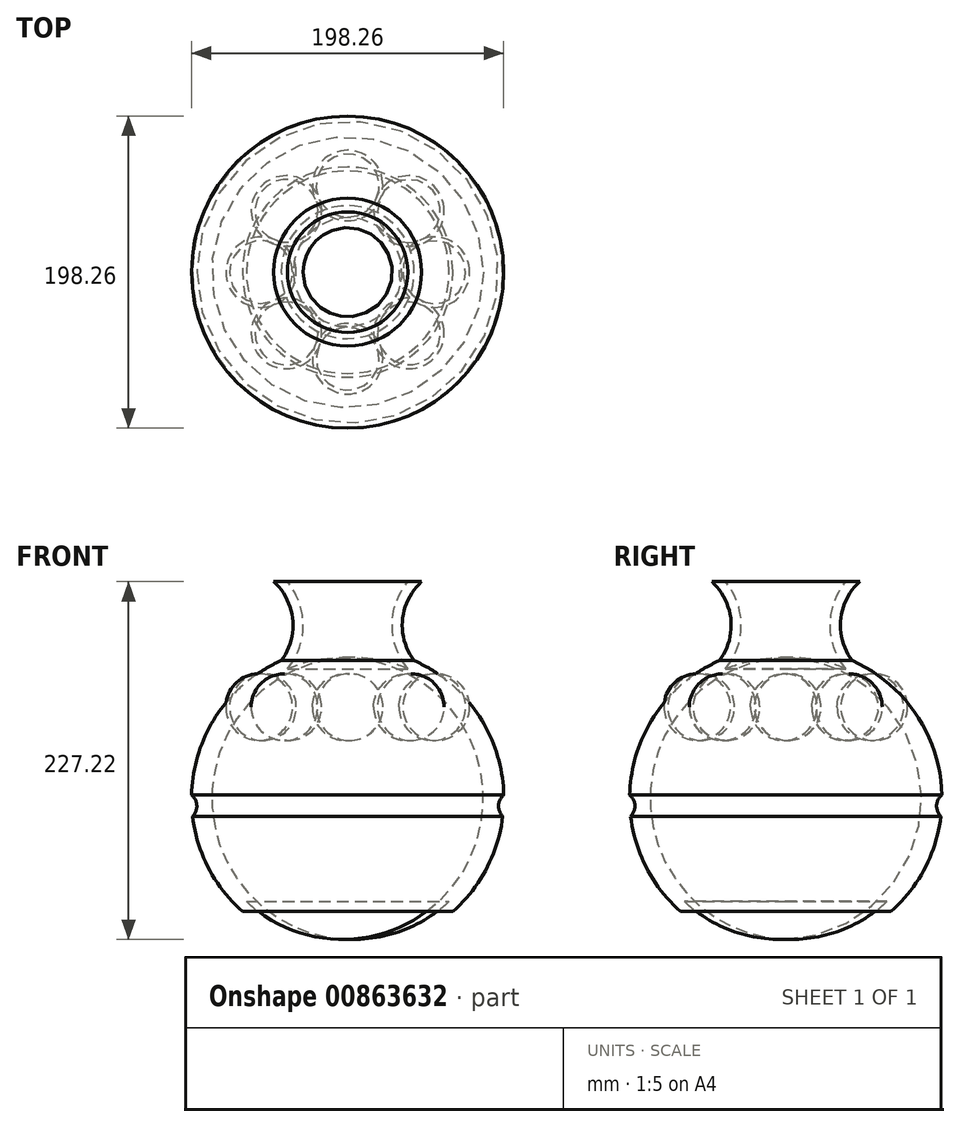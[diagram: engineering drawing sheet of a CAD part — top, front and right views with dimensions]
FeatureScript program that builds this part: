
annotation { "Feature Type Name" : "Feature", "Feature Type Description" : "" }
export const myFeature = defineFeature(function(context is Context, id is Id, definition is map)
    precondition{}
    {
        {
            var Q0;
            Q0=qCreatedBy(makeId("Front.planeOp"),FACE);
            var sketch = newSketch(context, id + "F0", { "sketchPlane" : qUnion([Q0])});
            skLineSegment(sketch, "E0", {"start": v(0, 0) * mm, "end": v(0, 203.2) * mm});
            skLineSegment(sketch, "E1", {"start": v(0, 203.2) * mm, "end": v(38.23, 203.2) * mm});
            skArc(sketch, "E2", {"start": v(38.23, 203.2) * mm, "mid": v(28.32, 175.53) * mm, "end": v(38.23, 147.86) * mm});
            skLineSegment(sketch, "E3", {"start": v(64.33, 0) * mm, "end": v(0, 0) * mm});
            skArc(sketch, "E4", {"start": v(64.33, 0) * mm, "mid": v(91.44, 81.02) * mm, "end": v(38.23, 147.86) * mm});
            skSolve(sketch);
        }
        {
            var Q0;
            Q0 = qSketchRegion(id + "F0", true);
            var Q1;
            Q1=sQuery(id+"F0.wireOp",EDGE,"E0");
            revolve(context, id + "F1", {"surfaceOperationType" : NewSurfaceOperationType.NEW, "entities" : qUnion([Q0]), "axis" : qUnion([Q1]), "revolveType" : RevolveType.FULL});
        }
        {
            var Q0;
            Q0=qCreatedBy(makeId("Front.planeOp"),FACE);
            var sketch = newSketch(context, id + "F2", { "sketchPlane" : qUnion([Q0])});
            skArc(sketch, "E5", {"start": v(176.67, 88.82) * mm, "mid": v(154.28, 67.68) * mm, "end": v(176.67, 46.53) * mm});
            skLineSegment(sketch, "E6", {"start": v(176.67, 88.82) * mm, "end": v(176.67, 46.53) * mm});
            skSolve(sketch);
        }
        {
            var Q0;
            Q0 = qSketchRegion(id + "F2", true);
            var Q1;
            Q1=sQuery(id+"F2.wireOp",EDGE,"E6");
            revolve(context, id + "F3", {"surfaceOperationType" : NewSurfaceOperationType.NEW, "entities" : qUnion([Q0]), "axis" : qUnion([Q1]), "revolveType" : RevolveType.FULL});
        }
        {
            var Q0;
            Q0=makeQuery(id+"F3.opRevolve","SWEPT_BODY",BODY,{"disambiguationData":[OSD([sQuery(id+"F2.wireOp",EDGE,"E5"),sQuery(id+"F2.wireOp",EDGE,"E6")])]});
            transform(context, id + "F4", {"entities" : qUnion([Q0]), "transformType" : TransformType.TRANSLATION_3D, "dx" : -121.67 * mm, "dy" : 0 * mm, "dz" : 55.88 * mm, "makeCopy" : false});
        }
        {
            var Q0;
            Q0=makeQuery(id+"F3.opRevolve","SWEPT_BODY",BODY,{"disambiguationData":[OSD([sQuery(id+"F2.wireOp",EDGE,"E5"),sQuery(id+"F2.wireOp",EDGE,"E6")])]});
            var Q1;
            Q1=makeQuery(id+"F1.opRevolve","SWEPT_EDGE",EDGE,{"disambiguationData":[OSD([sQuery(id+"F0.wireOp",EDGE,"E1"),sQuery(id+"F0.wireOp",EDGE,"E2")])]});
            circularPattern(context, id + "F5", {"entities" : qUnion([Q0]), "axis" : qUnion([Q1]), "angle" : 360 * degree, "instanceCount" : 8, "equalSpace" : true});
        }
        {
            var Q0;
            Q0=makeQuery(id+"F1.opRevolve","SWEPT_FACE",FACE,{"disambiguationData":[OSD([sQuery(id+"F0.wireOp",EDGE,"E1")])]});
            shell(context, id + "F6", {"entities" : qUnion([Q0]), "thickness" : 6.35 * mm, "oppositeDirection" : true});
        }
        {
            var Q0;
            Q0=qCreatedBy(makeId("Front.planeOp"),FACE);
            var sketch = newSketch(context, id + "F7", { "sketchPlane" : qUnion([Q0])});
            skArc(sketch, "E7", {"start": v(110.55, 75.75) * mm, "mid": v(104.23, 69.43) * mm, "end": v(110.55, 63.1) * mm});
            skLineSegment(sketch, "E8", {"start": v(110.55, 75.75) * mm, "end": v(110.55, 63.1) * mm});
            skSolve(sketch);
        }
        {
            var Q0;
            Q0 = qSketchRegion(id + "F7", true);
            var Q1;
            Q1=sQuery(id+"F7.wireOp",EDGE,"E8");
            revolve(context, id + "F8", {"surfaceOperationType" : NewSurfaceOperationType.NEW, "entities" : qUnion([Q0]), "axis" : qUnion([Q1]), "revolveType" : RevolveType.FULL});
        }
        {
            var Q0;
            Q0=makeQuery(id+"F8.opRevolve","SWEPT_BODY",BODY,{"disambiguationData":[OSD([sQuery(id+"F7.wireOp",EDGE,"E7"),sQuery(id+"F7.wireOp",EDGE,"E8")])]});
            transform(context, id + "F9", {"entities" : qUnion([Q0]), "transformType" : TransformType.TRANSLATION_3D, "dx" : -76.2 * mm, "dy" : 0 * mm, "dz" : 105.16 * mm, "makeCopy" : false});
        }
        {
            var Q0;
            Q0=makeQuery(id+"F8.opRevolve","SWEPT_BODY",BODY,{"disambiguationData":[OSD([sQuery(id+"F7.wireOp",EDGE,"E7"),sQuery(id+"F7.wireOp",EDGE,"E8")])]});
            var Q1;
            Q1=makeQuery(id+"F1.opRevolve","SWEPT_EDGE",EDGE,{"disambiguationData":[OSD([sQuery(id+"F0.wireOp",EDGE,"E1"),sQuery(id+"F0.wireOp",EDGE,"E2")])]});
            circularPattern(context, id + "F10", {"entities" : qUnion([Q0]), "axis" : qUnion([Q1]), "angle" : 360 * degree, "instanceCount" : 6, "equalSpace" : true});
        }
        {
            var Q0;
            Q0=qCreatedBy(makeId("Front.planeOp"),FACE);
            var sketch = newSketch(context, id + "F11", { "sketchPlane" : qUnion([Q0])});
            skCircle(sketch, "E9", {"center": v(-104.8, 60.62) * mm, "radius": 9.01 * mm});
            skSolve(sketch);
        }
        {
            var Q0;
            Q0=makeQuery(id+"F11.imprint","IMPRINT",FACE,{"disambiguationData":[TD([[makeQuery(id+"F11.imprint","IMPRINT",EDGE,{"derivedFrom":sQuery(id+"F11.wireOp",EDGE,"E9")}),1.0]])]});
            var Q1;
            Q1=makeQuery(id+"F1.opRevolve","SWEPT_FACE",FACE,{"disambiguationData":[OSD([sQuery(id+"F0.wireOp",EDGE,"E4")])]});
            revolve(context, id + "F12", {"operationType" : NewBodyOperationType.REMOVE, "surfaceOperationType" : NewSurfaceOperationType.NEW, "entities" : qUnion([Q0]), "axis" : qUnion([Q1]), "revolveType" : RevolveType.FULL, "oppositeDirection" : true});
        }
        {
            var Q0;
            Q0=makeQuery(id+"F8.opRevolve","SWEPT_BODY",BODY,{"disambiguationData":[OSD([sQuery(id+"F7.wireOp",EDGE,"E7"),sQuery(id+"F7.wireOp",EDGE,"E8")])]});
            var Q1;
            Q1=makeQuery(id+"F10.opPattern","COPY",BODY,{"derivedFrom":makeQuery(id+"F8.opRevolve","SWEPT_BODY",BODY,{"disambiguationData":[OSD([sQuery(id+"F7.wireOp",EDGE,"E7"),sQuery(id+"F7.wireOp",EDGE,"E8")])]}),"instanceName":"1"});
            var Q2;
            Q2=makeQuery(id+"F10.opPattern","COPY",BODY,{"derivedFrom":makeQuery(id+"F8.opRevolve","SWEPT_BODY",BODY,{"disambiguationData":[OSD([sQuery(id+"F7.wireOp",EDGE,"E7"),sQuery(id+"F7.wireOp",EDGE,"E8")])]}),"instanceName":"5"});
            var Q3;
            Q3=makeQuery(id+"F10.opPattern","COPY",BODY,{"derivedFrom":makeQuery(id+"F8.opRevolve","SWEPT_BODY",BODY,{"disambiguationData":[OSD([sQuery(id+"F7.wireOp",EDGE,"E7"),sQuery(id+"F7.wireOp",EDGE,"E8")])]}),"instanceName":"4"});
            var Q4;
            Q4=makeQuery(id+"F10.opPattern","COPY",BODY,{"derivedFrom":makeQuery(id+"F8.opRevolve","SWEPT_BODY",BODY,{"disambiguationData":[OSD([sQuery(id+"F7.wireOp",EDGE,"E7"),sQuery(id+"F7.wireOp",EDGE,"E8")])]}),"instanceName":"3"});
            var Q5;
            Q5=makeQuery(id+"F10.opPattern","COPY",BODY,{"derivedFrom":makeQuery(id+"F8.opRevolve","SWEPT_BODY",BODY,{"disambiguationData":[OSD([sQuery(id+"F7.wireOp",EDGE,"E7"),sQuery(id+"F7.wireOp",EDGE,"E8")])]}),"instanceName":"2"});
            var Q6;
            Q6=makeQuery(id+"F5.opPattern","COPY",BODY,{"derivedFrom":makeQuery(id+"F3.opRevolve","SWEPT_BODY",BODY,{"disambiguationData":[OSD([sQuery(id+"F2.wireOp",EDGE,"E5"),sQuery(id+"F2.wireOp",EDGE,"E6")])]}),"instanceName":"1"});
            booleanBodies(context, id + "F13", {"operationType" : BooleanOperationType.SUBTRACTION, "tools" : qUnion([Q0, Q1, Q2, Q3, Q4, Q5]), "targets" : qUnion([Q6])});
        }
    });
